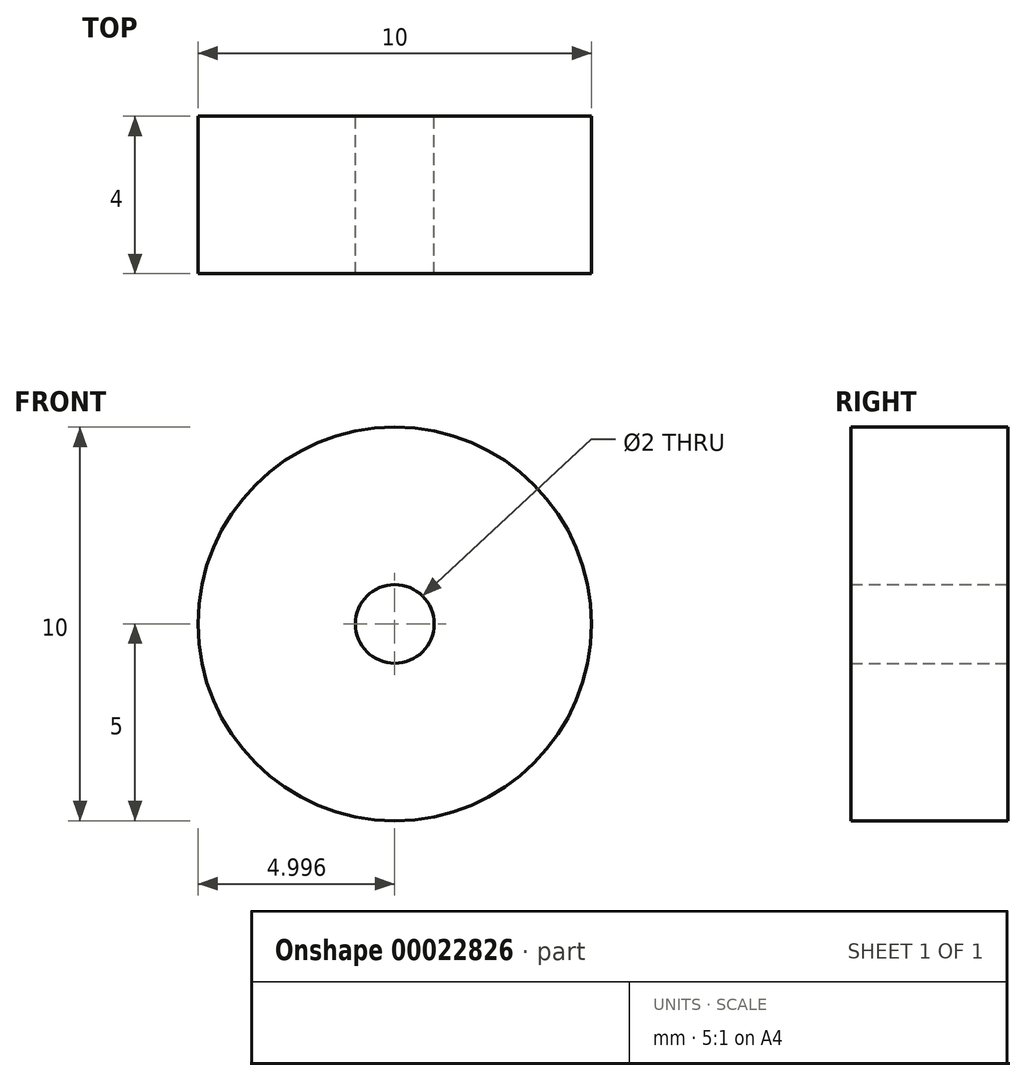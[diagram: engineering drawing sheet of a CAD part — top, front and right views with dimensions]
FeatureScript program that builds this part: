
annotation { "Feature Type Name" : "Feature", "Feature Type Description" : "" }
export const myFeature = defineFeature(function(context is Context, id is Id, definition is map)
    precondition{}
    {
        {
            var Q0;
            Q0=qCreatedBy(makeId("Front.planeOp"),FACE);
            var sketch = newSketch(context, id + "F0", { "sketchPlane" : qUnion([Q0])});
            skCircle(sketch, "E0", {"center": v(-34.52, 0) * mm, "radius": 5 * mm});
            skCircle(sketch, "E1", {"center": v(-34.52, 0) * mm, "radius": 1 * mm});
            skSolve(sketch);
        }
        {
            var Q0;
            Q0=makeQuery(id+"F0.imprint","IMPRINT",FACE,{"disambiguationData":[TD([[makeQuery(id+"F0.imprint","IMPRINT",EDGE,{"derivedFrom":sQuery(id+"F0.wireOp",EDGE,"E0")}),1.0]])]});
            extrude(context, id + "F1", {"entities" : qUnion([Q0]), "endBound" : BoundingType.SYMMETRIC, "depth" : 4 * mm});
        }
    });
